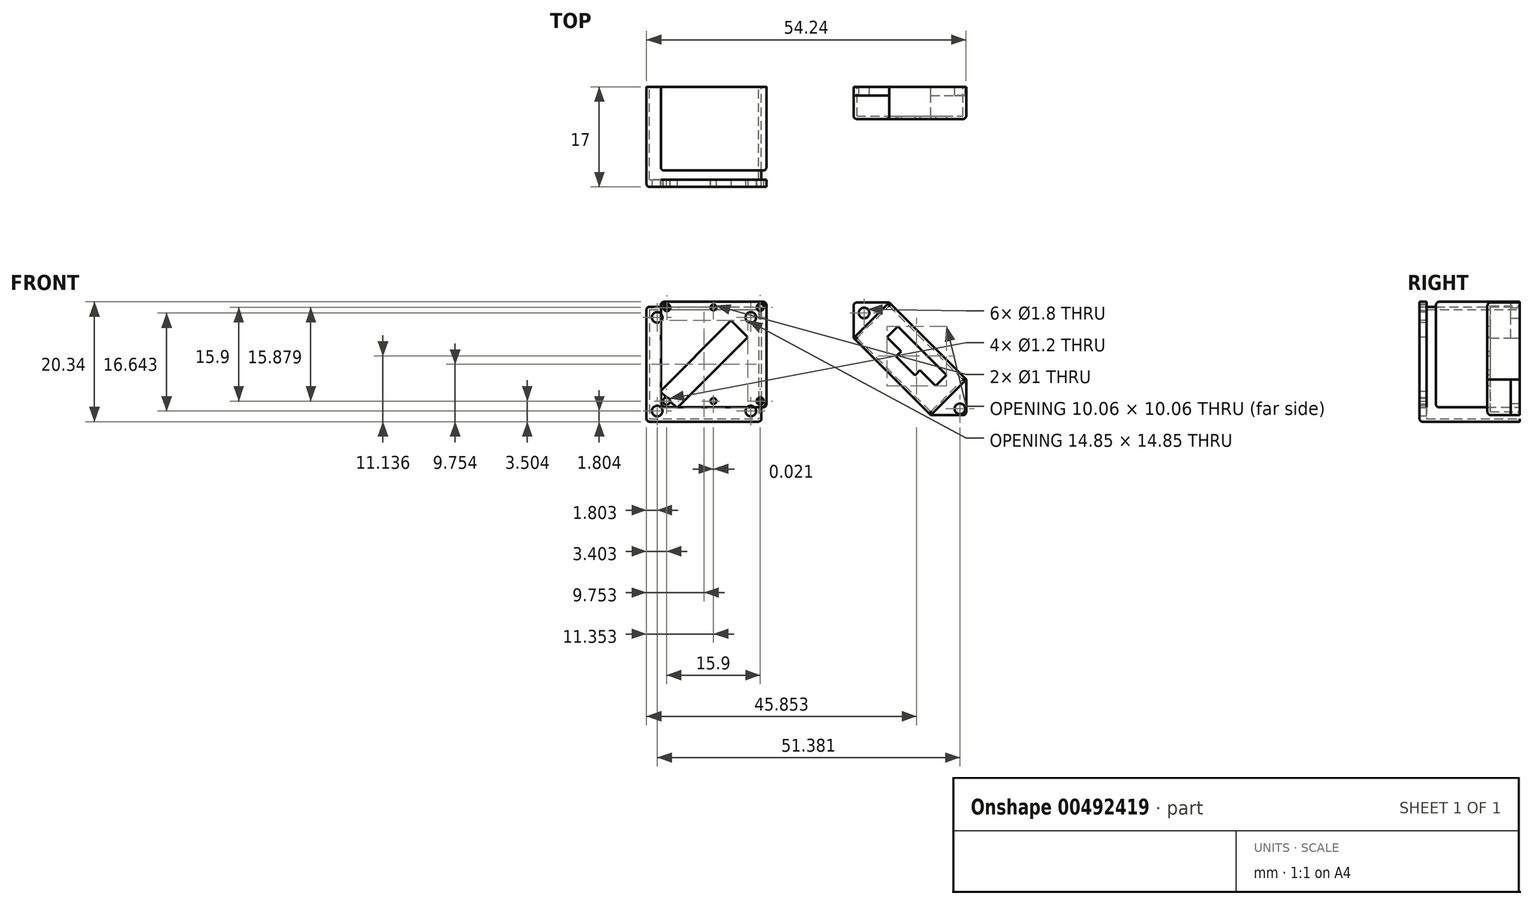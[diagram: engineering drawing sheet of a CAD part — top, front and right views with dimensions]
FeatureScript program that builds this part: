
annotation { "Feature Type Name" : "Feature", "Feature Type Description" : "" }
export const myFeature = defineFeature(function(context is Context, id is Id, definition is map)
    precondition{}
    {
        {
            var Q0;
            Q0=qCreatedBy(makeId("Front.planeOp"),FACE);
            var sketch = newSketch(context, id + "F0", { "sketchPlane" : qUnion([Q0])});
            skLineSegment(sketch, "E0.bottom", {"start": v(-51.58, 25.75) * mm, "end": v(-32.08, 25.75) * mm});
            skLineSegment(sketch, "E0.top", {"start": v(-51.58, 6.25) * mm, "end": v(-32.08, 6.25) * mm});
            skLineSegment(sketch, "E0.left", {"start": v(-51.58, 25.75) * mm, "end": v(-51.58, 6.25) * mm});
            skLineSegment(sketch, "E0.right", {"start": v(-32.08, 25.75) * mm, "end": v(-32.08, 6.25) * mm});
            skLineSegment(sketch, "E1.0", {"start": v(-32.58, 25.25) * mm, "end": v(-32.58, 6.75) * mm});
            skLineSegment(sketch, "E1.1", {"start": v(-51.08, 25.25) * mm, "end": v(-32.58, 25.25) * mm});
            skLineSegment(sketch, "E1.2", {"start": v(-51.08, 25.25) * mm, "end": v(-51.08, 6.75) * mm});
            skLineSegment(sketch, "E1.3", {"start": v(-51.08, 6.75) * mm, "end": v(-32.58, 6.75) * mm});
            skSolve(sketch);
        }
        {
            var Q0;
            Q0=makeQuery(id+"F0.imprint","IMPRINT",FACE,{"disambiguationData":[TD([[makeQuery(id+"F0.imprint","IMPRINT",EDGE,{"derivedFrom":sQuery(id+"F0.wireOp",EDGE,"E1.0")}),-1.0]])]});
            var Q1;
            Q1=makeQuery(id+"F0.imprint","IMPRINT",FACE,{"disambiguationData":[TD([[makeQuery(id+"F0.imprint","IMPRINT",EDGE,{"derivedFrom":sQuery(id+"F0.wireOp",EDGE,"E0.bottom")}),-1.0]])]});
            extrude(context, id + "F1", {"entities" : qUnion([Q0, Q1]), "depth" : 17 * mm});
        }
        {
            var Q0;
            Q0=makeQuery(id+"F0.imprint","IMPRINT",FACE,{"disambiguationData":[TD([[makeQuery(id+"F0.imprint","IMPRINT",EDGE,{"derivedFrom":sQuery(id+"F0.wireOp",EDGE,"E1.0")}),-1.0]])]});
            extrude(context, id + "F2", {"entities" : qUnion([Q0]), "operationType" : NewBodyOperationType.REMOVE, "depth" : (17 - 1.2) * mm});
        }
        {
            var Q0;
            Q0=makeQuery(id+"F1.opExtrude","CAP_FACE",FACE,{"disambiguationData":[OSD([sQuery(id+"F0.wireOp",EDGE,"E0.bottom"),sQuery(id+"F0.wireOp",EDGE,"E0.top"),sQuery(id+"F0.wireOp",EDGE,"E0.left"),sQuery(id+"F0.wireOp",EDGE,"E0.right")])],"isStart":false});
            var sketch = newSketch(context, id + "F3", { "sketchPlane" : qUnion([Q0])});
            skPoint(sketch, "E2.middle", {"position": v(-41.83, 25.75) * mm});
            skLineSegment(sketch, "E3.bottom", {"start": v(-49.25, 11.4) * mm, "end": v(-46.42, 8.58) * mm});
            skLineSegment(sketch, "E3.top", {"start": v(-37.23, 23.43) * mm, "end": v(-34.4, 20.6) * mm});
            skLineSegment(sketch, "E3.left", {"start": v(-49.25, 11.4) * mm, "end": v(-37.23, 23.43) * mm});
            skLineSegment(sketch, "E3.right", {"start": v(-46.42, 8.58) * mm, "end": v(-34.4, 20.6) * mm});
            skPoint(sketch, "E3.middle", {"position": v(-41.83, 16) * mm});
            skPoint(sketch, "E3.middle.positionSnap0", {"position": v(-32.08, 16) * mm});
            skPoint(sketch, "E3.centerSnap0", {"position": v(-32.08, 16) * mm});
            skSolve(sketch);
        }
        {
            var Q0;
            Q0=makeQuery(id+"F3.imprint","IMPRINT",FACE,{"disambiguationData":[TD([[makeQuery(id+"F3.imprint","IMPRINT",EDGE,{"derivedFrom":sQuery(id+"F3.wireOp",EDGE,"E3.bottom")}),-1.0]])]});
            var sketch = newSketch(context, id + "F4", { "sketchPlane" : qUnion([Q0])});
            skLineSegment(sketch, "E4.0", {"start": v(-51.58, 25.75) * mm, "end": v(-32.08, 25.75) * mm});
            skLineSegment(sketch, "E4.1", {"start": v(-32.08, 25.75) * mm, "end": v(-32.08, 6.25) * mm});
            skLineSegment(sketch, "E4.2", {"start": v(-51.58, 25.75) * mm, "end": v(-51.58, 6.25) * mm});
            skLineSegment(sketch, "E4.3", {"start": v(-51.58, 6.25) * mm, "end": v(-32.08, 6.25) * mm});
            skPoint(sketch, "E5", {"position": v(-33.88, 23.95) * mm});
            skPoint(sketch, "E6", {"position": v(-49.78, 23.95) * mm});
            skPoint(sketch, "E7", {"position": v(-49.78, 8.05) * mm});
            skPoint(sketch, "E8", {"position": v(-33.88, 8.05) * mm});
            skSolve(sketch);
        }
        {
            var Q0;
            Q0=sQuery(id+"F4.wireOp",VERTEX,"E5");
            var Q1;
            Q1=sQuery(id+"F4.wireOp",VERTEX,"E6");
            var Q2;
            Q2=sQuery(id+"F4.wireOp",VERTEX,"E7");
            var Q3;
            Q3=sQuery(id+"F4.wireOp",VERTEX,"E8");
            var Q4;
            Q4=makeQuery(id+"F1.opExtrude","SWEPT_BODY",BODY,{"disambiguationData":[OSD([sQuery(id+"F0.wireOp",EDGE,"E0.bottom"),sQuery(id+"F0.wireOp",EDGE,"E0.top"),sQuery(id+"F0.wireOp",EDGE,"E0.left"),sQuery(id+"F0.wireOp",EDGE,"E0.right")])]});
            hole(context, id + "F5", {"style" : HoleStyle.SIMPLE, "endStyle" : HoleEndStyle.THROUGH, "holeDiameter" : 1.8 * mm, "isTappedThrough" : true, "tappedDepth" : 12 * mm, "tapClearance" : 3, "locations" : qUnion([Q0, Q1, Q2, Q3]), "scope" : qUnion([Q4])});
        }
        {
            var Q0;
            Q0=makeQuery(id+"F3.imprint","IMPRINT",FACE,{"disambiguationData":[TD([[makeQuery(id+"F3.imprint","IMPRINT",EDGE,{"derivedFrom":sQuery(id+"F3.wireOp",EDGE,"E3.bottom")}),1.0]])]});
            extrude(context, id + "F6", {"entities" : qUnion([Q0]), "operationType" : NewBodyOperationType.REMOVE, "oppositeDirection" : true, "depth" : 25 * mm});
        }
        {
            var Q0;
            Q0=qCreatedBy(makeId("Front.planeOp"),FACE);
            var sketch = newSketch(context, id + "F7", { "sketchPlane" : qUnion([Q0])});
            skLineSegment(sketch, "E9.bottom", {"start": v(-16.43, 20.45) * mm, "end": v(-10.42, 26.46) * mm});
            skLineSegment(sketch, "E9.top", {"start": v(-3.35, 7.37) * mm, "end": v(2.66, 13.38) * mm});
            skLineSegment(sketch, "E9.left", {"start": v(-16.43, 20.45) * mm, "end": v(-3.35, 7.37) * mm});
            skLineSegment(sketch, "E9.right", {"start": v(-10.42, 26.46) * mm, "end": v(2.66, 13.38) * mm});
            skLineSegment(sketch, "E10.top", {"start": v(-16.43, 26.46) * mm, "end": v(-10.42, 26.46) * mm});
            skLineSegment(sketch, "E10.left", {"start": v(-16.43, 20.45) * mm, "end": v(-16.43, 26.46) * mm});
            skLineSegment(sketch, "E11.bottom", {"start": v(-3.35, 7.37) * mm, "end": v(2.66, 7.37) * mm});
            skLineSegment(sketch, "E11.right", {"start": v(2.66, 7.37) * mm, "end": v(2.66, 13.38) * mm});
            skCircle(sketch, "E12", {"center": v(-14.66, 24.7) * mm, "radius": 0.9 * mm});
            skCircle(sketch, "E13", {"center": v(1.6, 8.43) * mm, "radius": 0.9 * mm});
            skSolve(sketch);
        }
        {
            var Q0;
            Q0=makeQuery(id+"F7.imprint","IMPRINT",FACE,{"disambiguationData":[TD([[makeQuery(id+"F7.imprint","IMPRINT",EDGE,{"derivedFrom":sQuery(id+"F7.wireOp",EDGE,"E9.bottom")}),1.0]])]});
            var Q1;
            Q1=makeQuery(id+"F7.imprint","IMPRINT",FACE,{"disambiguationData":[TD([[makeQuery(id+"F7.imprint","IMPRINT",EDGE,{"derivedFrom":sQuery(id+"F7.wireOp",EDGE,"E9.top")}),-1.0]])]});
            var Q2;
            Q2=makeQuery(id+"F7.imprint","IMPRINT",FACE,{"disambiguationData":[TD([[makeQuery(id+"F7.imprint","IMPRINT",EDGE,{"derivedFrom":sQuery(id+"F7.wireOp",EDGE,"E9.bottom")}),-1.0]])]});
            extrude(context, id + "F8", {"entities" : qUnion([Q0, Q1, Q2]), "depth" : 1.5 * mm});
        }
        {
            var Q0;
            Q0=makeQuery(id+"F8.opExtrude","CAP_FACE",FACE,{"disambiguationData":[OSD([sQuery(id+"F7.wireOp",EDGE,"E9.left"),sQuery(id+"F7.wireOp",EDGE,"E9.right"),sQuery(id+"F7.wireOp",EDGE,"E10.top"),sQuery(id+"F7.wireOp",EDGE,"E10.left"),sQuery(id+"F7.wireOp",EDGE,"E11.bottom"),sQuery(id+"F7.wireOp",EDGE,"E11.right"),sQuery(id+"F7.wireOp",EDGE,"E12"),sQuery(id+"F7.wireOp",EDGE,"E13")])],"isStart":false});
            var sketch = newSketch(context, id + "F9", { "sketchPlane" : qUnion([Q0])});
            skLineSegment(sketch, "E14.0", {"start": v(-16.43, 20.45) * mm, "end": v(-10.42, 26.46) * mm});
            skLineSegment(sketch, "E14.1", {"start": v(-10.42, 26.46) * mm, "end": v(2.66, 13.38) * mm});
            skLineSegment(sketch, "E14.2", {"start": v(-16.43, 20.45) * mm, "end": v(-3.35, 7.37) * mm});
            skLineSegment(sketch, "E14.3", {"start": v(-3.35, 7.37) * mm, "end": v(2.66, 13.38) * mm});
            skSolve(sketch);
        }
        {
            var Q0;
            Q0=makeQuery(id+"F9.imprint","IMPRINT",FACE,{"disambiguationData":[TD([[makeQuery(id+"F9.imprint","IMPRINT",EDGE,{"derivedFrom":sQuery(id+"F9.wireOp",EDGE,"E14.0")}),-1.0]])]});
            extrude(context, id + "F10", {"entities" : qUnion([Q0]), "operationType" : NewBodyOperationType.ADD, "depth" : 4 * mm});
        }
        {
            var Q0;
            Q0=makeQuery(id+"F7.imprint","IMPRINT",FACE,{"disambiguationData":[TD([[makeQuery(id+"F7.imprint","IMPRINT",EDGE,{"derivedFrom":sQuery(id+"F7.wireOp",EDGE,"E9.bottom")}),-1.0]])]});
            var sketch = newSketch(context, id + "F11", { "sketchPlane" : qUnion([Q0])});
            skLineSegment(sketch, "E15.0", {"start": v(-3.35, 7.37) * mm, "end": v(2.66, 13.38) * mm});
            skLineSegment(sketch, "E15.1", {"start": v(-16.43, 20.45) * mm, "end": v(-3.35, 7.37) * mm});
            skLineSegment(sketch, "E15.2", {"start": v(-10.42, 26.46) * mm, "end": v(2.66, 13.38) * mm});
            skLineSegment(sketch, "E15.3", {"start": v(-16.43, 20.45) * mm, "end": v(-10.42, 26.46) * mm});
            skLineSegment(sketch, "E16.0", {"start": v(-10.42, 25.9) * mm, "end": v(2.1, 13.38) * mm});
            skLineSegment(sketch, "E16.1", {"start": v(-15.86, 20.45) * mm, "end": v(-10.42, 25.9) * mm});
            skLineSegment(sketch, "E16.2", {"start": v(-15.86, 20.45) * mm, "end": v(-3.35, 7.94) * mm});
            skLineSegment(sketch, "E16.3", {"start": v(-3.35, 7.94) * mm, "end": v(2.1, 13.38) * mm});
            skSolve(sketch);
        }
        {
            var Q0;
            Q0=makeQuery(id+"F11.imprint","IMPRINT",FACE,{"disambiguationData":[TD([[makeQuery(id+"F11.imprint","IMPRINT",EDGE,{"derivedFrom":sQuery(id+"F11.wireOp",EDGE,"E16.0")}),-1.0]])]});
            extrude(context, id + "F12", {"entities" : qUnion([Q0]), "operationType" : NewBodyOperationType.REMOVE, "depth" : 5 * mm});
        }
        {
            var Q0;
            Q0=makeQuery(id+"F10.opExtrude","CAP_FACE",FACE,{"disambiguationData":[OSD([sQuery(id+"F9.wireOp",EDGE,"E14.0"),sQuery(id+"F9.wireOp",EDGE,"E14.1"),sQuery(id+"F9.wireOp",EDGE,"E14.2"),sQuery(id+"F9.wireOp",EDGE,"E14.3")])],"isStart":false});
            var sketch = newSketch(context, id + "F13", { "sketchPlane" : qUnion([Q0])});
            skLineSegment(sketch, "E17.bottom", {"start": v(-10.76, 20.6) * mm, "end": v(-8.94, 22.42) * mm});
            skLineSegment(sketch, "E17.top", {"start": v(-2.52, 12.35) * mm, "end": v(-0.7, 14.18) * mm});
            skLineSegment(sketch, "E17.left", {"start": v(-10.76, 20.6) * mm, "end": v(-8.36, 18.2) * mm});
            skLineSegment(sketch, "E18.0", {"start": v(-9.22, 17.33) * mm, "end": v(-6.03, 14.13) * mm});
            skLineSegment(sketch, "E19", {"start": v(-6.03, 14.13) * mm, "end": v(-5.16, 15) * mm});
            skLineSegment(sketch, "E20", {"start": v(-9.22, 17.33) * mm, "end": v(-8.36, 18.2) * mm});
            skLineSegment(sketch, "E21.trimOffspring", {"start": v(-5.16, 15) * mm, "end": v(-2.52, 12.35) * mm});
            skLineSegment(sketch, "E22", {"start": v(-8.94, 22.42) * mm, "end": v(-0.7, 14.18) * mm});
            skSolve(sketch);
        }
        {
            var Q0;
            Q0=makeQuery(id+"F13.imprint","IMPRINT",FACE,{"disambiguationData":[TD([[makeQuery(id+"F13.imprint","IMPRINT",EDGE,{"derivedFrom":sQuery(id+"F13.wireOp",EDGE,"E17.bottom")}),-1.0]])]});
            extrude(context, id + "F14", {"entities" : qUnion([Q0]), "operationType" : NewBodyOperationType.REMOVE, "oppositeDirection" : true, "depth" : 25 * mm});
        }
        {
            var Q0;
            Q0=makeQuery(id+"F1.opExtrude","CAP_EDGE",EDGE,{"disambiguationData":[OSD([sQuery(id+"F0.wireOp",EDGE,"E0.top")])],"isStart":false});
            var Q1;
            Q1=makeQuery(id+"F1.opExtrude","SWEPT_EDGE",EDGE,{"disambiguationData":[OSD([sQuery(id+"F0.wireOp",EDGE,"E0.top"),sQuery(id+"F0.wireOp",EDGE,"E0.left")])]});
            var Q2;
            Q2=makeQuery(id+"F1.opExtrude","CAP_EDGE",EDGE,{"disambiguationData":[OSD([sQuery(id+"F0.wireOp",EDGE,"E0.left")])],"isStart":false});
            var Q3;
            Q3=makeQuery(id+"F1.opExtrude","CAP_EDGE",EDGE,{"disambiguationData":[OSD([sQuery(id+"F0.wireOp",EDGE,"E0.right")])],"isStart":false});
            var Q4;
            Q4=makeQuery(id+"F1.opExtrude","SWEPT_EDGE",EDGE,{"disambiguationData":[OSD([sQuery(id+"F0.wireOp",EDGE,"E0.top"),sQuery(id+"F0.wireOp",EDGE,"E0.right")])]});
            var Q5;
            Q5=makeQuery(id+"F1.opExtrude","SWEPT_EDGE",EDGE,{"disambiguationData":[OSD([sQuery(id+"F0.wireOp",EDGE,"E0.bottom"),sQuery(id+"F0.wireOp",EDGE,"E0.right")])]});
            var Q6;
            Q6=makeQuery(id+"F1.opExtrude","CAP_EDGE",EDGE,{"disambiguationData":[OSD([sQuery(id+"F0.wireOp",EDGE,"E0.bottom")])],"isStart":false});
            var Q7;
            Q7=makeQuery(id+"F1.opExtrude","SWEPT_EDGE",EDGE,{"disambiguationData":[OSD([sQuery(id+"F0.wireOp",EDGE,"E0.bottom"),sQuery(id+"F0.wireOp",EDGE,"E0.left")])]});
            var Q8;
            Q8=makeQuery(id+"F10.opExtrude","CAP_EDGE",EDGE,{"disambiguationData":[OSD([sQuery(id+"F9.wireOp",EDGE,"E14.2")])],"isStart":false});
            var Q9;
            Q9=makeQuery(id+"F10.opExtrude","CAP_EDGE",EDGE,{"disambiguationData":[OSD([sQuery(id+"F9.wireOp",EDGE,"E14.3")])],"isStart":false});
            var Q10;
            Q10=makeQuery(id+"F8.opExtrude","SWEPT_EDGE",EDGE,{"disambiguationData":[OSD([sQuery(id+"F7.wireOp",EDGE,"E11.bottom"),sQuery(id+"F7.wireOp",EDGE,"E11.right")])]});
            var Q11;
            Q11=makeQuery(id+"F10.opExtrude","CAP_EDGE",EDGE,{"disambiguationData":[OSD([sQuery(id+"F9.wireOp",EDGE,"E14.1")])],"isStart":false});
            var Q12;
            Q12=makeQuery(id+"F8.opExtrude","SWEPT_EDGE",EDGE,{"disambiguationData":[OSD([sQuery(id+"F7.wireOp",EDGE,"E10.top"),sQuery(id+"F7.wireOp",EDGE,"E10.left")])]});
            var Q13;
            Q13=makeQuery(id+"F10.opExtrude","CAP_EDGE",EDGE,{"disambiguationData":[OSD([sQuery(id+"F9.wireOp",EDGE,"E14.0")])],"isStart":false});
            fillet(context, id + "F15", {"entities" : qUnion([Q0, Q1, Q2, Q3, Q4, Q5, Q6, Q7, Q8, Q9, Q10, Q11, Q12, Q13]), "radius" : .5 * mm, "tangentPropagation" : true, "allowEdgeOverflow" : false});
        }
        {
            var Q0;
            Q0=makeQuery(id+"F2.boolean.opBoolean","COPY",FACE,{"derivedFrom":makeQuery(id+"F2.opExtrude","CAP_FACE",FACE,{"disambiguationData":[OSD([sQuery(id+"F0.wireOp",EDGE,"E1.0"),sQuery(id+"F0.wireOp",EDGE,"E1.1"),sQuery(id+"F0.wireOp",EDGE,"E1.2"),sQuery(id+"F0.wireOp",EDGE,"E1.3")])],"isStart":false})});
            var sketch = newSketch(context, id + "F16", { "sketchPlane" : qUnion([Q0])});
            skLineSegment(sketch, "E23.bottom", {"start": v(31.24, 26.6) * mm, "end": v(49.14, 26.6) * mm});
            skLineSegment(sketch, "E23.top", {"start": v(31.24, 8.7) * mm, "end": v(49.14, 8.7) * mm});
            skLineSegment(sketch, "E23.left", {"start": v(31.24, 26.6) * mm, "end": v(31.24, 8.7) * mm});
            skLineSegment(sketch, "E23.right", {"start": v(49.14, 26.6) * mm, "end": v(49.14, 8.7) * mm});
            skSolve(sketch);
        }
        {
            var Q0;
            Q0 = qSketchRegion(id + "F16", true);
            extrude(context, id + "F17", {"entities" : qUnion([Q0]), "oppositeDirection" : true, "depth" : 1.2 * mm});
        }
        {
            var Q0;
            Q0=makeQuery(id+"F17.opExtrude","CAP_FACE",FACE,{"disambiguationData":[OSD([sQuery(id+"F16.wireOp",EDGE,"E23.bottom"),sQuery(id+"F16.wireOp",EDGE,"E23.top"),sQuery(id+"F16.wireOp",EDGE,"E23.left"),sQuery(id+"F16.wireOp",EDGE,"E23.right")])],"isStart":true});
            var sketch = newSketch(context, id + "F18", { "sketchPlane" : qUnion([Q0])});
            skCircle(sketch, "E24.0", {"center": v(48.18, 9.75) * mm, "radius": 0.6 * mm});
            skCircle(sketch, "E24.1", {"center": v(48.14, 25.61) * mm, "radius": 0.6 * mm});
            skCircle(sketch, "E24.2", {"center": v(32.28, 25.65) * mm, "radius": 0.6 * mm});
            skCircle(sketch, "E24.3", {"center": v(32.28, 9.75) * mm, "radius": 0.6 * mm});
            skSolve(sketch);
        }
        {
            var Q0;
            Q0=makeQuery(id+"F18.imprint","IMPRINT",FACE,{"disambiguationData":[TD([[makeQuery(id+"F18.imprint","IMPRINT",EDGE,{"derivedFrom":sQuery(id+"F18.wireOp",EDGE,"E24.0")}),1.0]])]});
            var Q1;
            Q1=makeQuery(id+"F18.imprint","IMPRINT",FACE,{"disambiguationData":[TD([[makeQuery(id+"F18.imprint","IMPRINT",EDGE,{"derivedFrom":sQuery(id+"F18.wireOp",EDGE,"E24.3")}),1.0]])]});
            var Q2;
            Q2=makeQuery(id+"F18.imprint","IMPRINT",FACE,{"disambiguationData":[TD([[makeQuery(id+"F18.imprint","IMPRINT",EDGE,{"derivedFrom":sQuery(id+"F18.wireOp",EDGE,"E24.2")}),1.0]])]});
            var Q3;
            Q3=makeQuery(id+"F18.imprint","IMPRINT",FACE,{"disambiguationData":[TD([[makeQuery(id+"F18.imprint","IMPRINT",EDGE,{"derivedFrom":sQuery(id+"F18.wireOp",EDGE,"E24.1")}),1.0]])]});
            extrude(context, id + "F19", {"entities" : qUnion([Q0, Q1, Q2, Q3]), "operationType" : NewBodyOperationType.REMOVE, "oppositeDirection" : true, "depth" : 2 * mm});
        }
        {
            var Q0;
            Q0=makeQuery(id+"F17.opExtrude","CAP_FACE",FACE,{"disambiguationData":[OSD([sQuery(id+"F16.wireOp",EDGE,"E23.bottom"),sQuery(id+"F16.wireOp",EDGE,"E23.top"),sQuery(id+"F16.wireOp",EDGE,"E23.left"),sQuery(id+"F16.wireOp",EDGE,"E23.right")])],"isStart":true});
            var sketch = newSketch(context, id + "F20", { "sketchPlane" : qUnion([Q0])});
            skPoint(sketch, "E25", {"position": v(40.2, 25.63) * mm});
            skPoint(sketch, "E26", {"position": v(40.23, 9.75) * mm});
            skSolve(sketch);
        }
        {
            var Q0;
            Q0=sQuery(id+"F20.wireOp",VERTEX,"E25");
            var Q1;
            Q1=sQuery(id+"F20.wireOp",VERTEX,"E26");
            var Q2;
            Q2=makeQuery(id+"F17.opExtrude","SWEPT_BODY",BODY,{"disambiguationData":[OSD([sQuery(id+"F16.wireOp",EDGE,"E23.bottom"),sQuery(id+"F16.wireOp",EDGE,"E23.top"),sQuery(id+"F16.wireOp",EDGE,"E23.left"),sQuery(id+"F16.wireOp",EDGE,"E23.right")])]});
            hole(context, id + "F21", {"style" : HoleStyle.SIMPLE, "endStyle" : HoleEndStyle.THROUGH, "holeDiameter" : 1 * mm, "isTappedThrough" : true, "tappedDepth" : 12 * mm, "tapClearance" : 3, "locations" : qUnion([Q0, Q1]), "scope" : qUnion([Q2])});
        }
        {
            var Q0;
            Q0=qCreatedBy(makeId("Front.planeOp"),FACE);
            var sketch = newSketch(context, id + "F22", { "sketchPlane" : qUnion([Q0])});
            skLineSegment(sketch, "E27.0", {"start": v(-49.14, 26.6) * mm, "end": v(-49.14, 8.7) * mm});
            skLineSegment(sketch, "E27.1", {"start": v(-31.24, 26.6) * mm, "end": v(-49.14, 26.6) * mm});
            skLineSegment(sketch, "E27.2", {"start": v(-31.24, 26.6) * mm, "end": v(-31.24, 8.7) * mm});
            skLineSegment(sketch, "E27.3", {"start": v(-31.24, 8.7) * mm, "end": v(-49.14, 8.7) * mm});
            skSolve(sketch);
        }
        {
            var Q0;
            Q0 = qSketchRegion(id + "F22", true);
            extrude(context, id + "F23", {"entities" : qUnion([Q0]), "depth" : 14.2 * mm});
        }
        {
            var Q0;
            Q0=makeQuery(id+"F23.opExtrude","SWEPT_EDGE",EDGE,{"disambiguationData":[OSD([sQuery(id+"F22.wireOp",EDGE,"E27.0"),sQuery(id+"F22.wireOp",EDGE,"E27.1")])]});
            var Q1;
            Q1=makeQuery(id+"F23.opExtrude","SWEPT_EDGE",EDGE,{"disambiguationData":[OSD([sQuery(id+"F22.wireOp",EDGE,"E27.0"),sQuery(id+"F22.wireOp",EDGE,"E27.3")])]});
            var Q2;
            Q2=makeQuery(id+"F23.opExtrude","SWEPT_EDGE",EDGE,{"disambiguationData":[OSD([sQuery(id+"F22.wireOp",EDGE,"E27.1"),sQuery(id+"F22.wireOp",EDGE,"E27.2")])]});
            var Q3;
            Q3=makeQuery(id+"F23.opExtrude","SWEPT_EDGE",EDGE,{"disambiguationData":[OSD([sQuery(id+"F22.wireOp",EDGE,"E27.2"),sQuery(id+"F22.wireOp",EDGE,"E27.3")])]});
            var Q4;
            Q4=makeQuery(id+"F23.opExtrude","CAP_EDGE",EDGE,{"disambiguationData":[OSD([sQuery(id+"F22.wireOp",EDGE,"E27.3")])],"isStart":false});
            var Q5;
            Q5=makeQuery(id+"F23.opExtrude","CAP_EDGE",EDGE,{"disambiguationData":[OSD([sQuery(id+"F22.wireOp",EDGE,"E27.0")])],"isStart":false});
            var Q6;
            Q6=makeQuery(id+"F23.opExtrude","CAP_EDGE",EDGE,{"disambiguationData":[OSD([sQuery(id+"F22.wireOp",EDGE,"E27.1")])],"isStart":false});
            var Q7;
            Q7=makeQuery(id+"F23.opExtrude","CAP_EDGE",EDGE,{"disambiguationData":[OSD([sQuery(id+"F22.wireOp",EDGE,"E27.2")])],"isStart":false});
            fillet(context, id + "F24", {"entities" : qUnion([Q0, Q1, Q2, Q3, Q4, Q5, Q6, Q7]), "radius" : .5 * mm, "tangentPropagation" : true, "allowEdgeOverflow" : false});
        }
        {
            var Q0;
            Q0=makeQuery(id+"F17.opExtrude","SWEPT_EDGE",EDGE,{"disambiguationData":[OSD([sQuery(id+"F16.wireOp",EDGE,"E23.top"),sQuery(id+"F16.wireOp",EDGE,"E23.left")])]});
            var Q1;
            Q1=makeQuery(id+"F17.opExtrude","SWEPT_EDGE",EDGE,{"disambiguationData":[OSD([sQuery(id+"F0.wireOp",EDGE,"E1.0"),sQuery(id+"F0.wireOp",EDGE,"E1.1"),sQuery(id+"F0.wireOp",EDGE,"E1.2"),sQuery(id+"F0.wireOp",EDGE,"E1.3"),sQuery(id+"F5.hole-2.sketch.wireOp",EDGE,"core_line_2"),sQuery(id+"F16.wireOp",EDGE,"E23.top"),sQuery(id+"F16.wireOp",EDGE,"E23.right")])]});
            var Q2;
            Q2=makeQuery(id+"F17.opExtrude","SWEPT_EDGE",EDGE,{"disambiguationData":[OSD([sQuery(id+"F16.wireOp",EDGE,"E23.bottom"),sQuery(id+"F16.wireOp",EDGE,"E23.right")])]});
            var Q3;
            Q3=makeQuery(id+"F17.opExtrude","SWEPT_EDGE",EDGE,{"disambiguationData":[OSD([sQuery(id+"F16.wireOp",EDGE,"E23.bottom"),sQuery(id+"F16.wireOp",EDGE,"E23.left")])]});
            fillet(context, id + "F25", {"entities" : qUnion([Q0, Q1, Q2, Q3]), "radius" : 1 * mm, "tangentPropagation" : true, "allowEdgeOverflow" : false});
        }
    });
